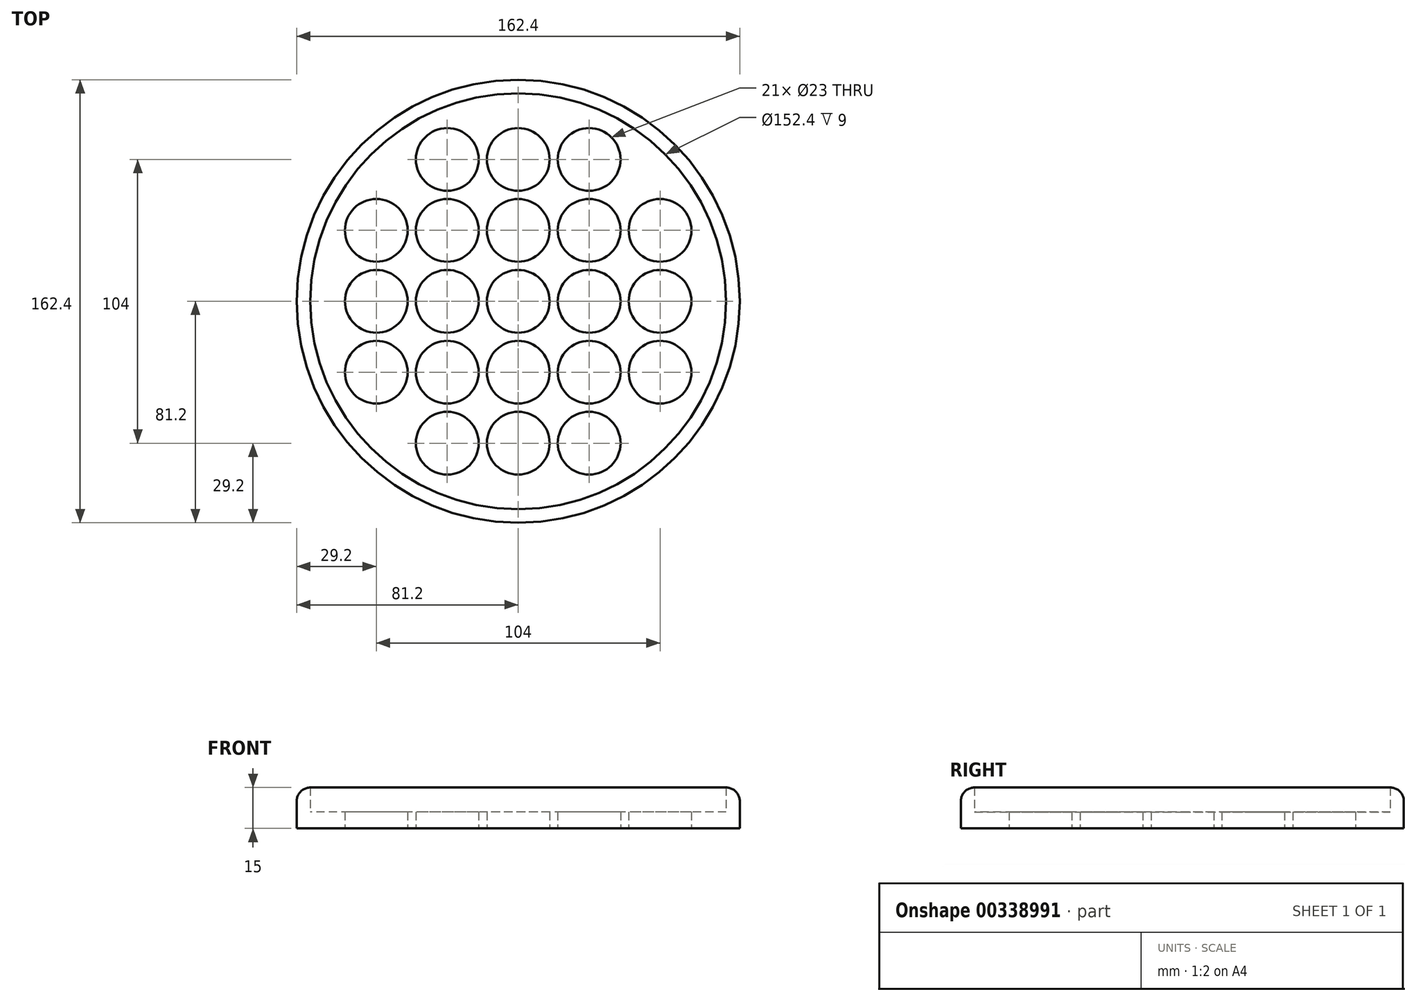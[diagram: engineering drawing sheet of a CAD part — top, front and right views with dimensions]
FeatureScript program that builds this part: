
annotation { "Feature Type Name" : "Feature", "Feature Type Description" : "" }
export const myFeature = defineFeature(function(context is Context, id is Id, definition is map)
    precondition{}
    {
        {
            var Q0;
            Q0=qCreatedBy(makeId("Top.planeOp"),FACE);
            var sketch = newSketch(context, id + "F0", { "sketchPlane" : qUnion([Q0])});
            skCircle(sketch, "E0", {"center": v(0, 0) * mm, "radius": 76.2 * mm});
            skCircle(sketch, "E1", {"center": v(0, 0) * mm, "radius": 11.5 * mm});
            skLineSegment(sketch, "E2", {"start": v(-76.2, 0) * mm, "end": v(76.2, 0) * mm, "construction": true});
            skCircle(sketch, "E3.0.1.0", {"center": v(0, 26) * mm, "radius": 11.5 * mm});
            skCircle(sketch, "E3.0.2.0", {"center": v(0, 52) * mm, "radius": 11.5 * mm});
            skCircle(sketch, "E3.1.0.0", {"center": v(26, 0) * mm, "radius": 11.5 * mm});
            skCircle(sketch, "E3.1.1.0", {"center": v(26, 26) * mm, "radius": 11.5 * mm});
            skCircle(sketch, "E3.1.2.0", {"center": v(26, 52) * mm, "radius": 11.5 * mm});
            skCircle(sketch, "E3.2.0.0", {"center": v(52, 0) * mm, "radius": 11.5 * mm});
            skCircle(sketch, "E3.2.1.0", {"center": v(52, 26) * mm, "radius": 11.5 * mm});
            skLineSegment(sketch, "E3.direction1", {"start": v(0, 0) * mm, "end": v(26, 0) * mm, "construction": true});
            skLineSegment(sketch, "E3.direction2", {"start": v(0, 0) * mm, "end": v(0, 26) * mm, "construction": true});
            skCircle(sketch, "E4.1.0.0", {"center": v(-26, 0) * mm, "radius": 11.5 * mm});
            skCircle(sketch, "E4.2.0.0", {"center": v(-52, 0) * mm, "radius": 11.5 * mm});
            skLineSegment(sketch, "E4.direction1", {"start": v(0, 0) * mm, "end": v(-26, 0) * mm, "construction": true});
            skCircle(sketch, "E5.0.1.0", {"center": v(-52, 26) * mm, "radius": 11.5 * mm});
            skCircle(sketch, "E5.0.1.1", {"center": v(-26, 26) * mm, "radius": 11.5 * mm});
            skCircle(sketch, "E5.0.2.1", {"center": v(-26, 52) * mm, "radius": 11.5 * mm});
            skCircle(sketch, "E5.1.1.0", {"center": v(-52, 26) * mm, "radius": 11.5 * mm});
            skCircle(sketch, "E5.1.1.1", {"center": v(-26, 26) * mm, "radius": 11.5 * mm});
            skCircle(sketch, "E5.1.2.1", {"center": v(-26, 52) * mm, "radius": 11.5 * mm});
            skCircle(sketch, "E5.2.1.0", {"center": v(-52, 26) * mm, "radius": 11.5 * mm});
            skCircle(sketch, "E5.2.1.1", {"center": v(-26, 26) * mm, "radius": 11.5 * mm});
            skCircle(sketch, "E5.2.2.1", {"center": v(-26, 52) * mm, "radius": 11.5 * mm});
            skLineSegment(sketch, "E5.direction1", {"start": v(-52, 0) * mm, "end": v(-52, 0) * mm});
            skLineSegment(sketch, "E5.direction2", {"start": v(-52, 0) * mm, "end": v(-52, 26) * mm, "construction": true});
            skCircle(sketch, "E6.0.1.0", {"center": v(-52, -26) * mm, "radius": 11.5 * mm});
            skCircle(sketch, "E6.0.1.1", {"center": v(-26, -26) * mm, "radius": 11.5 * mm});
            skCircle(sketch, "E6.0.1.2", {"center": v(0, -26) * mm, "radius": 11.5 * mm});
            skCircle(sketch, "E6.0.1.3", {"center": v(26, -26) * mm, "radius": 11.5 * mm});
            skCircle(sketch, "E6.0.1.4", {"center": v(52, -26) * mm, "radius": 11.5 * mm});
            skCircle(sketch, "E6.0.2.1", {"center": v(-26, -52) * mm, "radius": 11.5 * mm});
            skCircle(sketch, "E6.0.2.2", {"center": v(0, -52) * mm, "radius": 11.5 * mm});
            skCircle(sketch, "E6.0.2.3", {"center": v(26, -52) * mm, "radius": 11.5 * mm});
            skLineSegment(sketch, "E6.direction1", {"start": v(-52, 0) * mm, "end": v(-40.3, 0) * mm, "construction": true});
            skLineSegment(sketch, "E6.direction2", {"start": v(-52, 0) * mm, "end": v(-52, -26) * mm, "construction": true});
            skSolve(sketch);
        }
        {
            var Q0;
            Q0=makeQuery(id+"F0.imprint","IMPRINT",FACE,{"disambiguationData":[TD([[makeQuery(id+"F0.imprint","IMPRINT",EDGE,{"derivedFrom":sQuery(id+"F0.wireOp",EDGE,"E0")}),1.0]])]});
            extrude(context, id + "F1", {"entities" : qUnion([Q0]), "depth" : 6 * mm});
        }
        {
            var Q0;
            Q0=makeQuery(id+"F1.opExtrude","CAP_FACE",FACE,{"disambiguationData":[OSD([sQuery(id+"F0.wireOp",EDGE,"E0"),sQuery(id+"F0.wireOp",EDGE,"E1"),sQuery(id+"F0.wireOp",EDGE,"E3.0.1.0"),sQuery(id+"F0.wireOp",EDGE,"E3.0.2.0"),sQuery(id+"F0.wireOp",EDGE,"E3.1.0.0"),sQuery(id+"F0.wireOp",EDGE,"E3.1.1.0"),sQuery(id+"F0.wireOp",EDGE,"E3.1.2.0"),sQuery(id+"F0.wireOp",EDGE,"E3.2.0.0"),sQuery(id+"F0.wireOp",EDGE,"E3.2.1.0"),sQuery(id+"F0.wireOp",EDGE,"E4.2.0.0"),sQuery(id+"F0.wireOp",EDGE,"E4.1.0.0"),sQuery(id+"F0.wireOp",EDGE,"E5.2.1.0"),sQuery(id+"F0.wireOp",EDGE,"E5.2.1.1"),sQuery(id+"F0.wireOp",EDGE,"E5.2.2.1"),sQuery(id+"F0.wireOp",EDGE,"E6.0.1.0"),sQuery(id+"F0.wireOp",EDGE,"E6.0.1.1"),sQuery(id+"F0.wireOp",EDGE,"E6.0.1.2"),sQuery(id+"F0.wireOp",EDGE,"E6.0.1.3"),sQuery(id+"F0.wireOp",EDGE,"E6.0.1.4"),sQuery(id+"F0.wireOp",EDGE,"E6.0.2.1"),sQuery(id+"F0.wireOp",EDGE,"E6.0.2.2"),sQuery(id+"F0.wireOp",EDGE,"E6.0.2.3")])],"isStart":true});
            var sketch = newSketch(context, id + "F2", { "sketchPlane" : qUnion([Q0])});
            skCircle(sketch, "E7.0", {"center": v(0, 0) * mm, "radius": 81.2 * mm});
            skSolve(sketch);
        }
        {
            var Q0;
            Q0=makeQuery(id+"F2.imprint","IMPRINT",FACE,{"disambiguationData":[TD([[makeQuery(id+"F2.imprint","IMPRINT",EDGE,{"derivedFrom":sQuery(id+"F2.wireOp",EDGE,"E7.0")}),1.0]])]});
            extrude(context, id + "F3", {"entities" : qUnion([Q0]), "operationType" : NewBodyOperationType.ADD, "oppositeDirection" : true, "depth" : 15 * mm});
        }
        {
            var Q0;
            Q0=makeQuery(id+"F3.opExtrude","CAP_EDGE",EDGE,{"disambiguationData":[OSD([sQuery(id+"F2.wireOp",EDGE,"E7.0")])],"isStart":false});
            fillet(context, id + "F4", {"entities" : qUnion([Q0]), "radius" : 5 * mm, "tangentPropagation" : true, "allowEdgeOverflow" : false});
        }
    });
